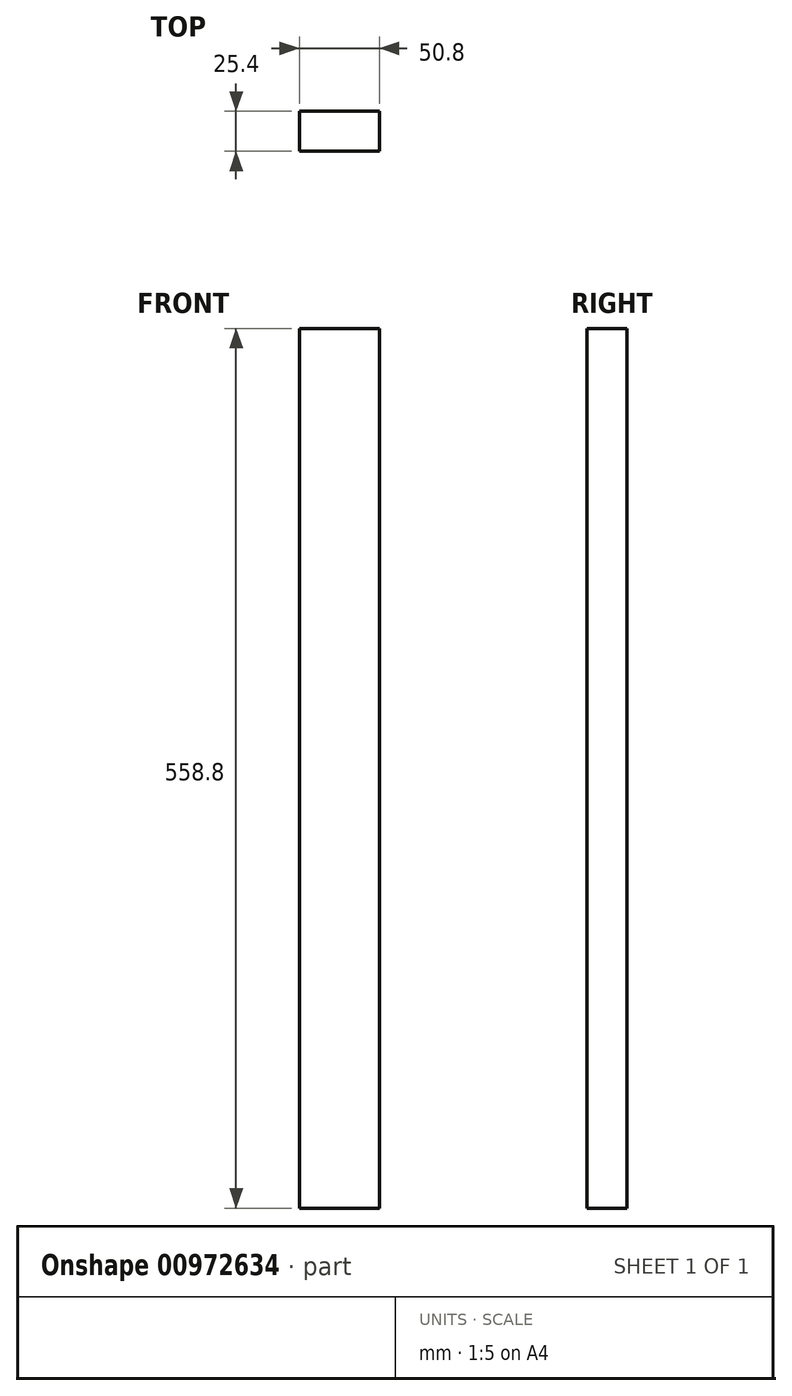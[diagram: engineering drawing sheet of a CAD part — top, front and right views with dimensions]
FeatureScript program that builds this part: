
annotation { "Feature Type Name" : "Feature", "Feature Type Description" : "" }
export const myFeature = defineFeature(function(context is Context, id is Id, definition is map)
    precondition{}
    {
        {
            var Q0;
            Q0=qCreatedBy(makeId("Top.planeOp"),FACE);
            var sketch = newSketch(context, id + "F0", { "sketchPlane" : qUnion([Q0])});
            skLineSegment(sketch, "E0.bottom", {"start": v(-149.74, 24) * mm, "end": v(-98.94, 24) * mm});
            skLineSegment(sketch, "E0.top", {"start": v(-149.74, -1.4) * mm, "end": v(-98.94, -1.4) * mm});
            skLineSegment(sketch, "E0.left", {"start": v(-149.74, 24) * mm, "end": v(-149.74, -1.4) * mm});
            skLineSegment(sketch, "E0.right", {"start": v(-98.94, 24) * mm, "end": v(-98.94, -1.4) * mm});
            skSolve(sketch);
        }
        {
            var Q0;
            Q0=makeQuery(id+"F0.imprint","IMPRINT",FACE,{"disambiguationData":[TD([[makeQuery(id+"F0.imprint","IMPRINT",EDGE,{"derivedFrom":sQuery(id+"F0.wireOp",EDGE,"E0.bottom")}),-1.0]])]});
            extrude(context, id + "F1", {"entities" : qUnion([Q0]), "depth" : 762 * mm, "offsetDistance" : 25.4 * mm});
        }
        {
            var Q0;
            Q0=makeQuery(id+"F1.opExtrude","CAP_FACE",FACE,{"disambiguationData":[OSD([sQuery(id+"F0.wireOp",EDGE,"E0.bottom"),sQuery(id+"F0.wireOp",EDGE,"E0.top"),sQuery(id+"F0.wireOp",EDGE,"E0.left"),sQuery(id+"F0.wireOp",EDGE,"E0.right")])],"isStart":true});
            extrude(context, id + "F2", {"entities" : qUnion([Q0]), "operationType" : NewBodyOperationType.REMOVE, "oppositeDirection" : true, "depth" : 25.4 * mm, "offsetDistance" : 25.4 * mm});
        }
        {
            var Q0;
            Q0=makeQuery(id+"F2.boolean.opBoolean","COPY",FACE,{"derivedFrom":makeQuery(id+"F2.opExtrude","CAP_FACE",FACE,{"disambiguationData":[OSD([sQuery(id+"F0.wireOp",EDGE,"E0.bottom"),sQuery(id+"F0.wireOp",EDGE,"E0.top"),sQuery(id+"F0.wireOp",EDGE,"E0.left"),sQuery(id+"F0.wireOp",EDGE,"E0.right")])],"isStart":false})});
            extrude(context, id + "F3", {"entities" : qUnion([Q0]), "operationType" : NewBodyOperationType.REMOVE, "oppositeDirection" : true, "depth" : 127 * mm, "offsetDistance" : 25.4 * mm});
        }
        {
            var Q0;
            Q0=makeQuery(id+"F3.boolean.opBoolean","COPY",FACE,{"derivedFrom":makeQuery(id+"F3.opExtrude","CAP_FACE",FACE,{"disambiguationData":[OSD([sQuery(id+"F0.wireOp",EDGE,"E0.bottom"),sQuery(id+"F0.wireOp",EDGE,"E0.top"),sQuery(id+"F0.wireOp",EDGE,"E0.left"),sQuery(id+"F0.wireOp",EDGE,"E0.right")])],"isStart":false})});
            extrude(context, id + "F4", {"entities" : qUnion([Q0]), "operationType" : NewBodyOperationType.REMOVE, "oppositeDirection" : true, "depth" : 101.6 * mm, "offsetDistance" : 25.4 * mm});
        }
        {
            var Q0;
            Q0=makeQuery(id+"F4.boolean.opBoolean","COPY",FACE,{"derivedFrom":makeQuery(id+"F4.opExtrude","CAP_FACE",FACE,{"disambiguationData":[OSD([sQuery(id+"F0.wireOp",EDGE,"E0.bottom"),sQuery(id+"F0.wireOp",EDGE,"E0.top"),sQuery(id+"F0.wireOp",EDGE,"E0.left"),sQuery(id+"F0.wireOp",EDGE,"E0.right")])],"isStart":false})});
            extrude(context, id + "F5", {"entities" : qUnion([Q0]), "operationType" : NewBodyOperationType.ADD, "depth" : 50.8 * mm, "offsetDistance" : 25.4 * mm});
        }
    });
